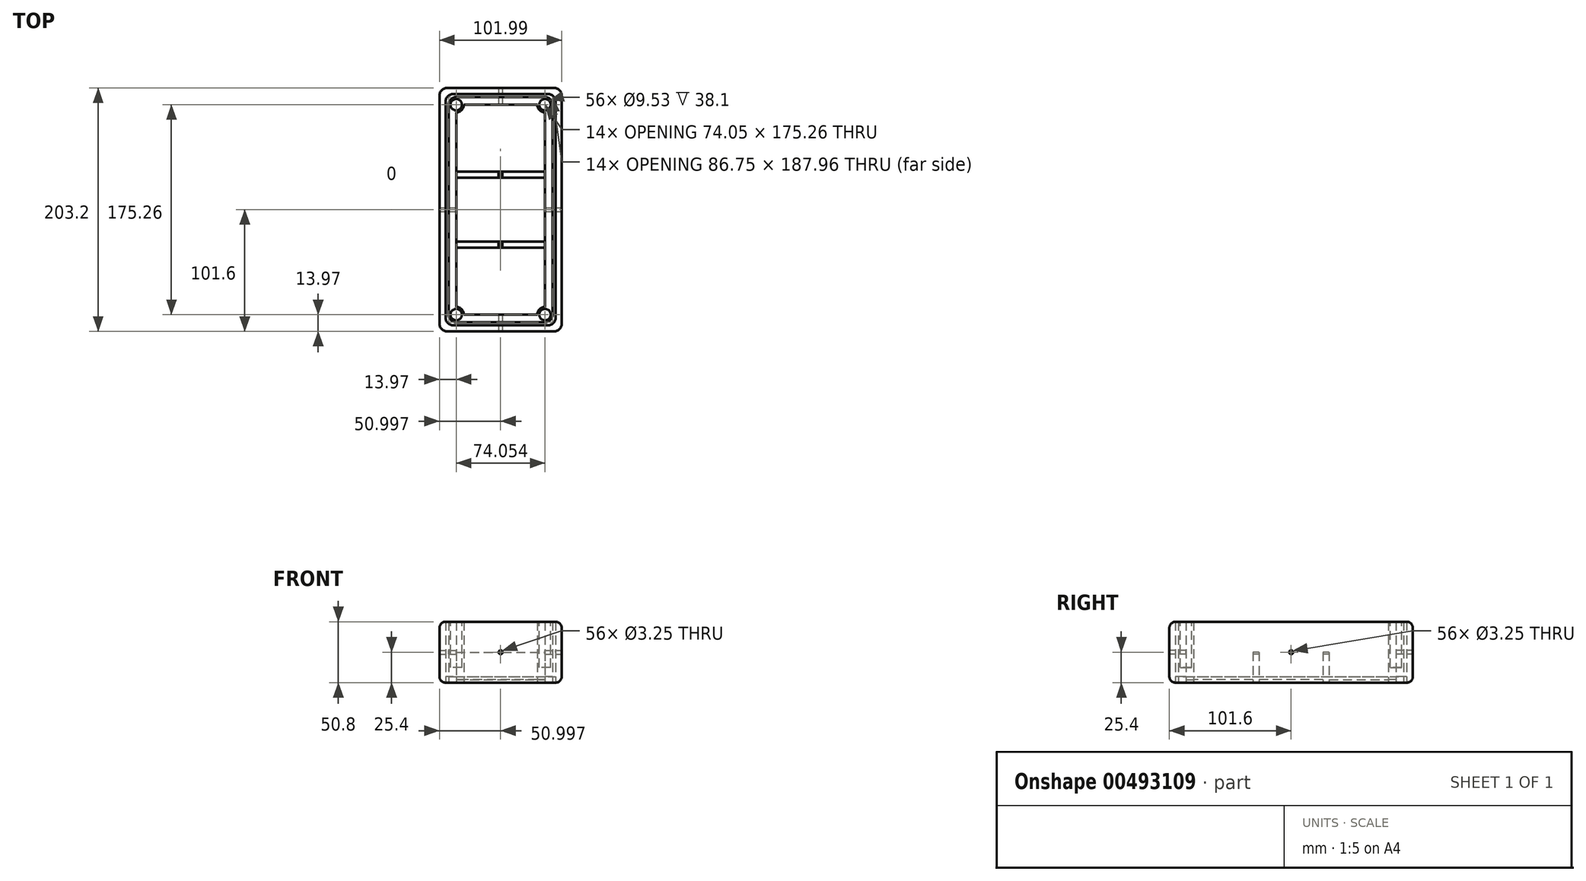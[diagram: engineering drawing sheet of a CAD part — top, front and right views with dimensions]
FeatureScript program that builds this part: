
annotation { "Feature Type Name" : "Feature", "Feature Type Description" : "" }
export const myFeature = defineFeature(function(context is Context, id is Id, definition is map)
    precondition{}
    {
        {
            var Q0;
            Q0=qCreatedBy(makeId("Top.planeOp"),FACE);
            var sketch = newSketch(context, id + "F0", { "sketchPlane" : qUnion([Q0])});
            skLineSegment(sketch, "E0.bottom", {"start": v(0, 0) * mm, "end": v(102, 0) * mm});
            skLineSegment(sketch, "E0.top", {"start": v(0, 203.2) * mm, "end": v(102, 203.2) * mm});
            skLineSegment(sketch, "E0.left", {"start": v(0, 0) * mm, "end": v(0, 203.2) * mm});
            skLineSegment(sketch, "E0.right", {"start": v(102, 0) * mm, "end": v(102, 203.2) * mm});
            skLineSegment(sketch, "E1.bottom", {"start": v(5.08, 5.08) * mm, "end": v(96.91, 5.08) * mm});
            skLineSegment(sketch, "E1.top", {"start": v(5.08, 198.12) * mm, "end": v(96.91, 198.12) * mm});
            skLineSegment(sketch, "E1.left", {"start": v(5.08, 5.08) * mm, "end": v(5.08, 198.12) * mm});
            skLineSegment(sketch, "E1.right", {"start": v(96.91, 5.08) * mm, "end": v(96.91, 198.12) * mm});
            skLineSegment(sketch, "E2.bottom", {"start": v(7.62, 7.62) * mm, "end": v(94.37, 7.62) * mm});
            skLineSegment(sketch, "E2.top", {"start": v(7.62, 195.58) * mm, "end": v(94.37, 195.58) * mm});
            skLineSegment(sketch, "E2.left", {"start": v(7.62, 7.62) * mm, "end": v(7.62, 195.58) * mm});
            skLineSegment(sketch, "E2.right", {"start": v(94.37, 7.62) * mm, "end": v(94.37, 195.58) * mm});
            skLineSegment(sketch, "E3.bottom", {"start": v(13.97, 13.97) * mm, "end": v(88.02, 13.97) * mm, "construction": true});
            skLineSegment(sketch, "E3.top", {"start": v(13.97, 189.23) * mm, "end": v(88.02, 189.23) * mm, "construction": true});
            skLineSegment(sketch, "E3.left", {"start": v(13.97, 13.97) * mm, "end": v(13.97, 189.23) * mm, "construction": true});
            skLineSegment(sketch, "E3.right", {"start": v(88.02, 13.97) * mm, "end": v(88.02, 189.23) * mm, "construction": true});
            skCircle(sketch, "E4", {"center": v(13.97, 189.23) * mm, "radius": 6.35 * mm, "construction": true});
            skCircle(sketch, "E5", {"center": v(88.02, 189.23) * mm, "radius": 6.35 * mm, "construction": true});
            skCircle(sketch, "E6", {"center": v(88.02, 13.97) * mm, "radius": 6.35 * mm, "construction": true});
            skCircle(sketch, "E7", {"center": v(13.97, 13.97) * mm, "radius": 6.35 * mm, "construction": true});
            skArc(sketch, "E8", {"start": v(13.97, 182.88) * mm, "mid": v(18.46, 184.74) * mm, "end": v(20.32, 189.23) * mm});
            skArc(sketch, "E9", {"start": v(81.67, 189.23) * mm, "mid": v(83.53, 184.74) * mm, "end": v(88.02, 182.88) * mm});
            skArc(sketch, "E10", {"start": v(88.02, 20.32) * mm, "mid": v(83.53, 18.46) * mm, "end": v(81.67, 13.97) * mm});
            skArc(sketch, "E11", {"start": v(20.32, 13.97) * mm, "mid": v(18.46, 18.46) * mm, "end": v(13.97, 20.32) * mm});
            skLineSegment(sketch, "E12", {"start": v(20.32, 189.23) * mm, "end": v(81.67, 189.23) * mm});
            skLineSegment(sketch, "E13", {"start": v(88.02, 182.88) * mm, "end": v(88.02, 20.32) * mm});
            skLineSegment(sketch, "E14", {"start": v(81.67, 13.97) * mm, "end": v(20.32, 13.97) * mm});
            skLineSegment(sketch, "E15", {"start": v(13.97, 20.32) * mm, "end": v(13.97, 182.88) * mm});
            skLineSegment(sketch, "E16.bottom", {"start": v(13.97, 128.27) * mm, "end": v(88.02, 128.27) * mm});
            skLineSegment(sketch, "E16.top", {"start": v(13.97, 133.35) * mm, "end": v(88.02, 133.35) * mm});
            skLineSegment(sketch, "E16.left", {"start": v(13.97, 128.27) * mm, "end": v(13.97, 133.35) * mm});
            skLineSegment(sketch, "E16.right", {"start": v(88.02, 128.27) * mm, "end": v(88.02, 133.35) * mm});
            skLineSegment(sketch, "E17.bottom", {"start": v(13.97, 74.93) * mm, "end": v(88.02, 74.93) * mm});
            skLineSegment(sketch, "E17.top", {"start": v(13.97, 69.85) * mm, "end": v(88.02, 69.85) * mm});
            skLineSegment(sketch, "E17.left", {"start": v(13.97, 69.85) * mm, "end": v(13.97, 74.93) * mm});
            skLineSegment(sketch, "E17.right", {"start": v(88.02, 69.85) * mm, "end": v(88.02, 74.93) * mm});
            skLineSegment(sketch, "E18", {"start": v(13.97, 130.81) * mm, "end": v(88.02, 130.81) * mm, "construction": true});
            skLineSegment(sketch, "E19", {"start": v(13.97, 72.4) * mm, "end": v(88.02, 72.4) * mm, "construction": true});
            skSolve(sketch);
        }
        {
            var Q0;
            Q0=makeQuery(id+"F0.imprint","IMPRINT",FACE,{"disambiguationData":[TD([[makeQuery(id+"F0.imprint","IMPRINT",EDGE,{"derivedFrom":sQuery(id+"F0.wireOp",EDGE,"E0.bottom")}),1.0]])]});
            var Q1;
            Q1=makeQuery(id+"F0.imprint","IMPRINT",FACE,{"disambiguationData":[TD([[makeQuery(id+"F0.imprint","IMPRINT",EDGE,{"derivedFrom":sQuery(id+"F0.wireOp",EDGE,"E2.bottom")}),1.0]])]});
            extrude(context, id + "F1", {"entities" : qUnion([Q0, Q1]), "depth" : 50.8 * mm});
        }
        {
            var Q0;
            Q0=makeQuery(id+"F0.imprint","IMPRINT",FACE,{"disambiguationData":[TD([[makeQuery(id+"F0.imprint","IMPRINT",EDGE,{"derivedFrom":sQuery(id+"F0.wireOp",EDGE,"E1.bottom")}),1.0]])]});
            extrude(context, id + "F2", {"entities" : qUnion([Q0]), "depth" : 5.08 * mm});
        }
        {
            var Q0;
            Q0=makeQuery(id+"F0.imprint","IMPRINT",FACE,{"disambiguationData":[TD([[makeQuery(id+"F0.imprint","IMPRINT",EDGE,{"derivedFrom":sQuery(id+"F0.wireOp",EDGE,"E16.bottom")}),1.0]])]});
            var Q1;
            Q1=makeQuery(id+"F0.imprint","IMPRINT",FACE,{"disambiguationData":[TD([[makeQuery(id+"F0.imprint","IMPRINT",EDGE,{"derivedFrom":sQuery(id+"F0.wireOp",EDGE,"E17.bottom")}),-1.0]])]});
            extrude(context, id + "F3", {"entities" : qUnion([Q0, Q1]), "depth" : 25.4 * mm});
        }
        {
            var Q0;
            Q0=makeQuery(id+"F1.opExtrude","SWEPT_EDGE",EDGE,{"disambiguationData":[OSD([sQuery(id+"F0.wireOp",EDGE,"E0.bottom"),sQuery(id+"F0.wireOp",EDGE,"E0.right")])]});
            var Q1;
            Q1=makeQuery(id+"F1.opExtrude","SWEPT_EDGE",EDGE,{"disambiguationData":[OSD([sQuery(id+"F0.wireOp",EDGE,"E0.bottom"),sQuery(id+"F0.wireOp",EDGE,"E0.left")])]});
            var Q2;
            Q2=makeQuery(id+"F1.opExtrude","SWEPT_EDGE",EDGE,{"disambiguationData":[OSD([sQuery(id+"F0.wireOp",EDGE,"E1.bottom"),sQuery(id+"F0.wireOp",EDGE,"E1.right")])]});
            var Q3;
            Q3=makeQuery(id+"F1.opExtrude","SWEPT_EDGE",EDGE,{"disambiguationData":[OSD([sQuery(id+"F0.wireOp",EDGE,"E2.bottom"),sQuery(id+"F0.wireOp",EDGE,"E2.right")])]});
            var Q4;
            Q4=makeQuery(id+"F1.opExtrude","SWEPT_EDGE",EDGE,{"disambiguationData":[OSD([sQuery(id+"F0.wireOp",EDGE,"E2.bottom"),sQuery(id+"F0.wireOp",EDGE,"E2.left")])]});
            var Q5;
            Q5=makeQuery(id+"F1.opExtrude","SWEPT_EDGE",EDGE,{"disambiguationData":[OSD([sQuery(id+"F0.wireOp",EDGE,"E1.bottom"),sQuery(id+"F0.wireOp",EDGE,"E1.left")])]});
            var Q6;
            Q6=makeQuery(id+"F1.opExtrude","SWEPT_EDGE",EDGE,{"disambiguationData":[OSD([sQuery(id+"F0.wireOp",EDGE,"E0.top"),sQuery(id+"F0.wireOp",EDGE,"E0.right")])]});
            var Q7;
            Q7=makeQuery(id+"F1.opExtrude","SWEPT_EDGE",EDGE,{"disambiguationData":[OSD([sQuery(id+"F0.wireOp",EDGE,"E0.top"),sQuery(id+"F0.wireOp",EDGE,"E0.left")])]});
            var Q8;
            Q8=makeQuery(id+"F1.opExtrude","SWEPT_EDGE",EDGE,{"disambiguationData":[OSD([sQuery(id+"F0.wireOp",EDGE,"E2.top"),sQuery(id+"F0.wireOp",EDGE,"E2.left")])]});
            var Q9;
            Q9=makeQuery(id+"F1.opExtrude","SWEPT_EDGE",EDGE,{"disambiguationData":[OSD([sQuery(id+"F0.wireOp",EDGE,"E2.top"),sQuery(id+"F0.wireOp",EDGE,"E2.right")])]});
            var Q10;
            Q10=makeQuery(id+"F1.opExtrude","SWEPT_EDGE",EDGE,{"disambiguationData":[OSD([sQuery(id+"F0.wireOp",EDGE,"E1.top"),sQuery(id+"F0.wireOp",EDGE,"E1.right")])]});
            var Q11;
            Q11=makeQuery(id+"F1.opExtrude","SWEPT_EDGE",EDGE,{"disambiguationData":[OSD([sQuery(id+"F0.wireOp",EDGE,"E1.top"),sQuery(id+"F0.wireOp",EDGE,"E1.left")])]});
            fillet(context, id + "F4", {"entities" : qUnion([Q0, Q1, Q2, Q3, Q4, Q5, Q6, Q7, Q8, Q9, Q10, Q11]), "radius" : 6.35 * mm, "tangentPropagation" : true, "allowEdgeOverflow" : false});
        }
        {
            var Q0;
            Q0=makeQuery(id+"F2.opExtrude","SWEPT_EDGE",EDGE,{"disambiguationData":[OSD([sQuery(id+"F0.wireOp",EDGE,"E2.bottom"),sQuery(id+"F0.wireOp",EDGE,"E2.left")])]});
            var Q1;
            Q1=makeQuery(id+"F2.opExtrude","SWEPT_EDGE",EDGE,{"disambiguationData":[OSD([sQuery(id+"F0.wireOp",EDGE,"E1.bottom"),sQuery(id+"F0.wireOp",EDGE,"E1.left")])]});
            var Q2;
            Q2=makeQuery(id+"F2.opExtrude","SWEPT_EDGE",EDGE,{"disambiguationData":[OSD([sQuery(id+"F0.wireOp",EDGE,"E2.bottom"),sQuery(id+"F0.wireOp",EDGE,"E2.right")])]});
            var Q3;
            Q3=makeQuery(id+"F2.opExtrude","SWEPT_EDGE",EDGE,{"disambiguationData":[OSD([sQuery(id+"F0.wireOp",EDGE,"E1.bottom"),sQuery(id+"F0.wireOp",EDGE,"E1.right")])]});
            var Q4;
            Q4=makeQuery(id+"F2.opExtrude","SWEPT_EDGE",EDGE,{"disambiguationData":[OSD([sQuery(id+"F0.wireOp",EDGE,"E2.top"),sQuery(id+"F0.wireOp",EDGE,"E2.left")])]});
            var Q5;
            Q5=makeQuery(id+"F2.opExtrude","SWEPT_EDGE",EDGE,{"disambiguationData":[OSD([sQuery(id+"F0.wireOp",EDGE,"E1.top"),sQuery(id+"F0.wireOp",EDGE,"E1.right")])]});
            var Q6;
            Q6=makeQuery(id+"F2.opExtrude","SWEPT_EDGE",EDGE,{"disambiguationData":[OSD([sQuery(id+"F0.wireOp",EDGE,"E2.top"),sQuery(id+"F0.wireOp",EDGE,"E2.right")])]});
            var Q7;
            Q7=makeQuery(id+"F2.opExtrude","SWEPT_EDGE",EDGE,{"disambiguationData":[OSD([sQuery(id+"F0.wireOp",EDGE,"E1.top"),sQuery(id+"F0.wireOp",EDGE,"E1.left")])]});
            fillet(context, id + "F5", {"entities" : qUnion([Q0, Q1, Q2, Q3, Q4, Q5, Q6, Q7]), "radius" : 6.35 * mm, "tangentPropagation" : true, "allowEdgeOverflow" : false});
        }
        {
            var Q0;
            Q0=makeQuery(id+"F1.opExtrude","SWEPT_FACE",FACE,{"disambiguationData":[OSD([sQuery(id+"F0.wireOp",EDGE,"E0.right")])]});
            var sketch = newSketch(context, id + "F6", { "sketchPlane" : qUnion([Q0])});
            skCircle(sketch, "E20", {"center": v(101.6, 25.4) * mm, "radius": 1.63 * mm});
            skLineSegment(sketch, "E21", {"start": v(6.35, 25.4) * mm, "end": v(196.85, 25.4) * mm, "construction": true});
            skLineSegment(sketch, "E22", {"start": v(101.6, 0) * mm, "end": v(101.6, 50.8) * mm, "construction": true});
            skSolve(sketch);
        }
        {
            var Q0;
            Q0=makeQuery(id+"F1.opExtrude","SWEPT_FACE",FACE,{"disambiguationData":[OSD([sQuery(id+"F0.wireOp",EDGE,"E0.bottom")])]});
            var sketch = newSketch(context, id + "F7", { "sketchPlane" : qUnion([Q0])});
            skLineSegment(sketch, "E23", {"start": v(6.35, 25.4) * mm, "end": v(95.64, 25.4) * mm, "construction": true});
            skLineSegment(sketch, "E24", {"start": v(51, 0) * mm, "end": v(51, 50.8) * mm, "construction": true});
            skCircle(sketch, "E25", {"center": v(51, 25.4) * mm, "radius": 1.63 * mm});
            skSolve(sketch);
        }
        {
            var Q0;
            Q0=makeQuery(id+"F6.imprint","IMPRINT",FACE,{"disambiguationData":[TD([[makeQuery(id+"F6.imprint","IMPRINT",EDGE,{"derivedFrom":sQuery(id+"F6.wireOp",EDGE,"E20")}),1.0]])]});
            extrude(context, id + "F8", {"entities" : qUnion([Q0]), "operationType" : NewBodyOperationType.REMOVE, "oppositeDirection" : true, "depth" : 127 * mm});
        }
        {
            var Q0;
            Q0=makeQuery(id+"F7.imprint","IMPRINT",FACE,{"disambiguationData":[TD([[makeQuery(id+"F7.imprint","IMPRINT",EDGE,{"derivedFrom":sQuery(id+"F7.wireOp",EDGE,"E25")}),1.0]])]});
            extrude(context, id + "F9", {"entities" : qUnion([Q0]), "operationType" : NewBodyOperationType.REMOVE, "oppositeDirection" : true, "depth" : 254 * mm});
        }
        {
            var Q0;
            Q0=makeQuery(id+"F1.opExtrude","CAP_FACE",FACE,{"disambiguationData":[OSD([sQuery(id+"F0.wireOp",EDGE,"E2.bottom"),sQuery(id+"F0.wireOp",EDGE,"E2.top"),sQuery(id+"F0.wireOp",EDGE,"E2.left"),sQuery(id+"F0.wireOp",EDGE,"E2.right"),sQuery(id+"F0.wireOp",EDGE,"E8"),sQuery(id+"F0.wireOp",EDGE,"E9"),sQuery(id+"F0.wireOp",EDGE,"E10"),sQuery(id+"F0.wireOp",EDGE,"E11"),sQuery(id+"F0.wireOp",EDGE,"E12"),sQuery(id+"F0.wireOp",EDGE,"E13"),sQuery(id+"F0.wireOp",EDGE,"E14"),sQuery(id+"F0.wireOp",EDGE,"E15"),sQuery(id+"F0.wireOp",EDGE,"E16.left"),sQuery(id+"F0.wireOp",EDGE,"E16.right"),sQuery(id+"F0.wireOp",EDGE,"E17.left"),sQuery(id+"F0.wireOp",EDGE,"E17.right")])],"isStart":false});
            var sketch = newSketch(context, id + "F10", { "sketchPlane" : qUnion([Q0])});
            skCircle(sketch, "E26", {"center": v(13.97, 189.23) * mm, "radius": 4.76 * mm});
            skCircle(sketch, "E27", {"center": v(88.02, 189.23) * mm, "radius": 4.76 * mm});
            skCircle(sketch, "E28", {"center": v(88.02, 13.97) * mm, "radius": 4.76 * mm});
            skCircle(sketch, "E29", {"center": v(13.97, 13.97) * mm, "radius": 4.76 * mm});
            skSolve(sketch);
        }
        {
            var Q0;
            Q0=makeQuery(id+"F10.imprint","IMPRINT",FACE,{"disambiguationData":[TD([[makeQuery(id+"F10.imprint","IMPRINT",EDGE,{"derivedFrom":sQuery(id+"F10.wireOp",EDGE,"E28")}),1.0]])]});
            var Q1;
            Q1=makeQuery(id+"F10.imprint","IMPRINT",FACE,{"disambiguationData":[TD([[makeQuery(id+"F10.imprint","IMPRINT",EDGE,{"derivedFrom":sQuery(id+"F10.wireOp",EDGE,"E29")}),1.0]])]});
            var Q2;
            Q2=makeQuery(id+"F10.imprint","IMPRINT",FACE,{"disambiguationData":[TD([[makeQuery(id+"F10.imprint","IMPRINT",EDGE,{"derivedFrom":sQuery(id+"F10.wireOp",EDGE,"E26")}),1.0]])]});
            var Q3;
            Q3=makeQuery(id+"F10.imprint","IMPRINT",FACE,{"disambiguationData":[TD([[makeQuery(id+"F10.imprint","IMPRINT",EDGE,{"derivedFrom":sQuery(id+"F10.wireOp",EDGE,"E27")}),1.0]])]});
            extrude(context, id + "F11", {"entities" : qUnion([Q0, Q1, Q2, Q3]), "operationType" : NewBodyOperationType.REMOVE, "oppositeDirection" : true, "depth" : 38.1 * mm});
        }
        {
            var Q0;
            {var subQ2=sQuery(id+"F0.wireOp",EDGE,"E10");Q0=makeQuery(id+"F0.imprint","IMPRINT",FACE,{"disambiguationData":[TD([[makeQuery(id+"F0.imprint","IMPRINT",EDGE,{"derivedFrom":subQ2}),-1.0]])]});}
            var Q1;
            {var subQ0=sQuery(id+"F0.wireOp",EDGE,"E16.bottom");Q1=makeQuery(id+"F0.imprint","IMPRINT",FACE,{"disambiguationData":[TD([[makeQuery(id+"F0.imprint","IMPRINT",EDGE,{"derivedFrom":subQ0}),-1.0]])]});}
            var Q2;
            {var subQ3=sQuery(id+"F0.wireOp",EDGE,"E8");Q2=makeQuery(id+"F0.imprint","IMPRINT",FACE,{"disambiguationData":[TD([[makeQuery(id+"F0.imprint","IMPRINT",EDGE,{"derivedFrom":subQ3}),-1.0]])]});}
            extrude(context, id + "F12", {"entities" : qUnion([Q0, Q1, Q2]), "depth" : 2.54 * mm});
        }
        {
            var Q0;
            Q0=makeQuery(id+"F1.opExtrude","CAP_EDGE",EDGE,{"disambiguationData":[OSD([sQuery(id+"F0.wireOp",EDGE,"E0.right")])],"isStart":true});
            var Q1;
            Q1=makeQuery(id+"F1.opExtrude","CAP_EDGE",EDGE,{"disambiguationData":[OSD([sQuery(id+"F0.wireOp",EDGE,"E0.right")])],"isStart":false});
            fillet(context, id + "F13", {"entities" : qUnion([Q0, Q1]), "radius" : 5.08 * mm, "tangentPropagation" : true, "allowEdgeOverflow" : false});
        }
    });
